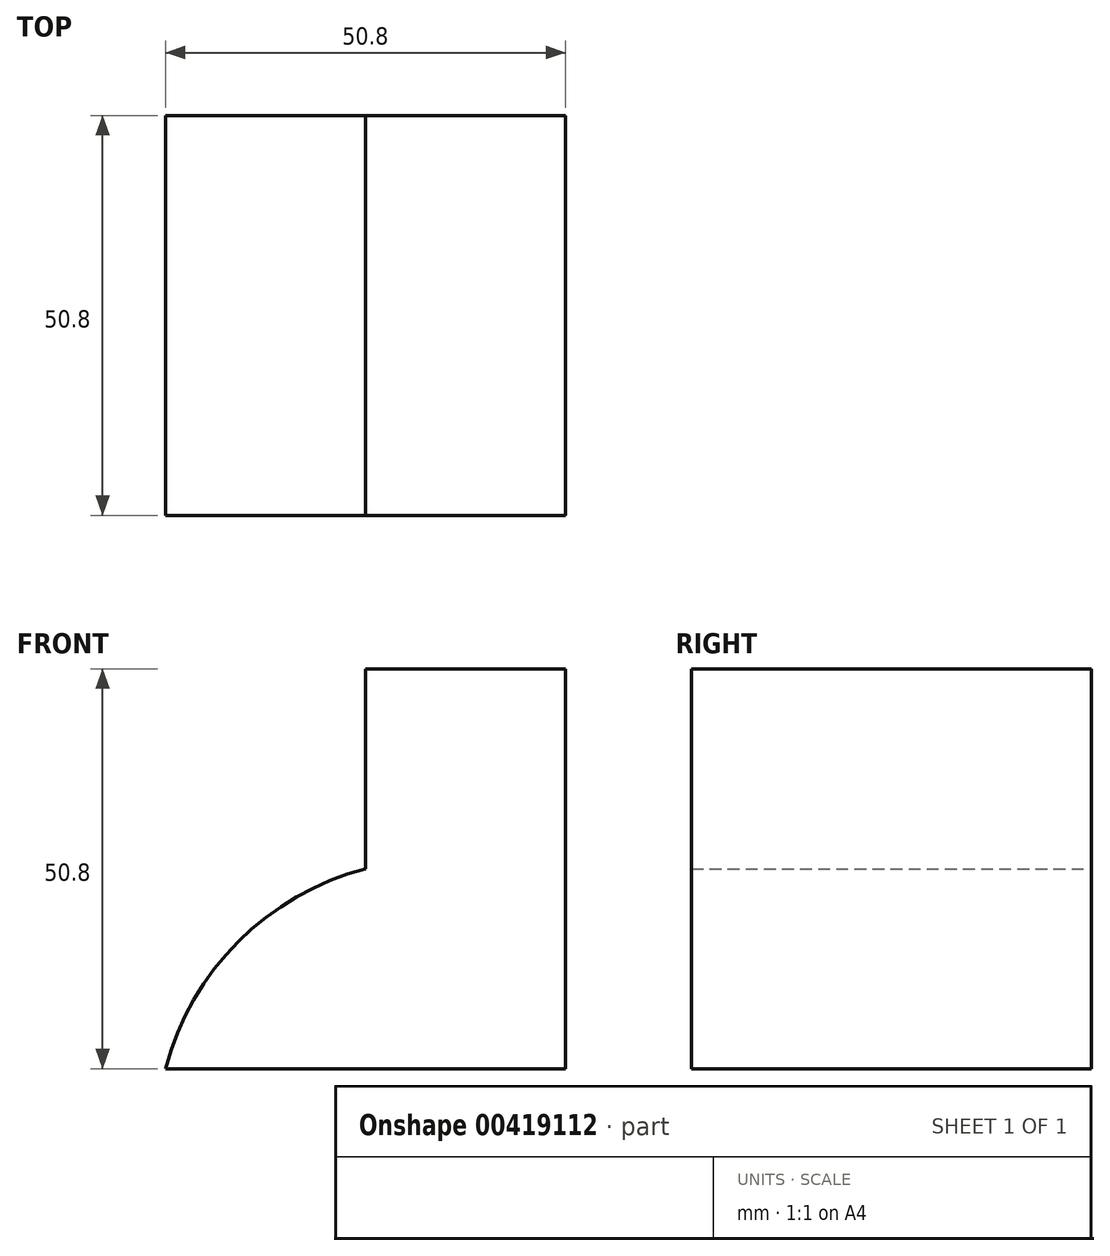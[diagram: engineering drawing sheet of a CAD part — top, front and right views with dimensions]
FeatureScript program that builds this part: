
annotation { "Feature Type Name" : "Feature", "Feature Type Description" : "" }
export const myFeature = defineFeature(function(context is Context, id is Id, definition is map)
    precondition{}
    {
        {
            var Q0;
            Q0=qCreatedBy(makeId("Front.planeOp"),FACE);
            var sketch = newSketch(context, id + "F0", { "sketchPlane" : qUnion([Q0])});
            skLineSegment(sketch, "E0", {"start": v(0, 0) * mm, "end": v(-50.8, 0) * mm});
            skLineSegment(sketch, "E1", {"start": v(0, 0) * mm, "end": v(0, 50.8) * mm});
            skLineSegment(sketch, "E2", {"start": v(0, 50.8) * mm, "end": v(-25.4, 50.8) * mm});
            skLineSegment(sketch, "E3", {"start": v(-25.4, 50.8) * mm, "end": v(-25.4, 25.4) * mm});
            skArc(sketch, "E4", {"start": v(-25.4, 25.4) * mm, "mid": v(-41.55, 16.15) * mm, "end": v(-50.8, 0) * mm});
            skSolve(sketch);
        }
        {
            var Q0;
            Q0 = qSketchRegion(id + "F0", true);
            extrude(context, id + "F1", {"entities" : qUnion([Q0]), "depth" : 50.8 * mm});
        }
    });
